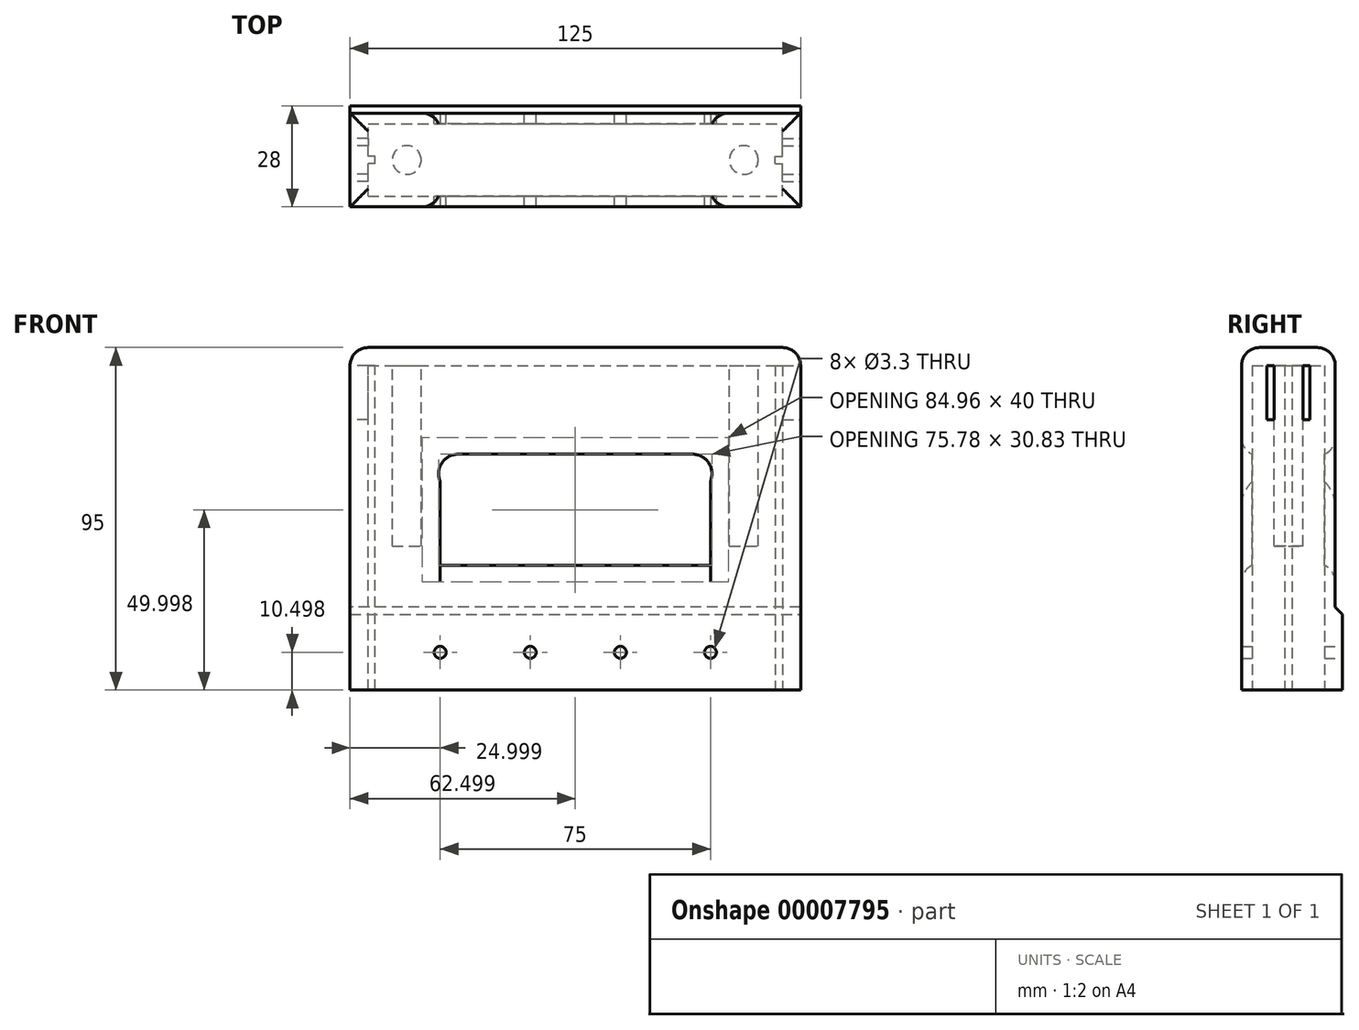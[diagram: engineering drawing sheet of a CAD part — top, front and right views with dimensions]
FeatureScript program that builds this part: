
annotation { "Feature Type Name" : "Feature", "Feature Type Description" : "" }
export const myFeature = defineFeature(function(context is Context, id is Id, definition is map)
    precondition{}
    {
        {
            var Q0;
            Q0=qCreatedBy(makeId("Front.planeOp"),FACE);
            var sketch = newSketch(context, id + "F0", { "sketchPlane" : qUnion([Q0])});
            skLineSegment(sketch, "E0.bottom", {"start": v(-53.4, 72.15) * mm, "end": v(71.6, 72.15) * mm});
            skLineSegment(sketch, "E0.top", {"start": v(-53.4, -22.85) * mm, "end": v(71.6, -22.85) * mm});
            skLineSegment(sketch, "E0.left", {"start": v(-53.4, 72.15) * mm, "end": v(-53.4, -22.85) * mm});
            skLineSegment(sketch, "E0.right", {"start": v(71.6, 72.15) * mm, "end": v(71.6, -22.85) * mm});
            skLineSegment(sketch, "E1.bottom", {"start": v(-28.4, 42.15) * mm, "end": v(46.6, 42.15) * mm});
            skLineSegment(sketch, "E1.top", {"start": v(-28.4, 12.15) * mm, "end": v(46.6, 12.15) * mm});
            skLineSegment(sketch, "E1.left", {"start": v(-28.4, 42.15) * mm, "end": v(-28.4, 12.15) * mm});
            skLineSegment(sketch, "E1.right", {"start": v(46.6, 42.15) * mm, "end": v(46.6, 12.15) * mm});
            skLineSegment(sketch, "E2", {"start": v(-28.4, 42.15) * mm, "end": v(-53.4, 42.15) * mm, "construction": true});
            skLineSegment(sketch, "E3", {"start": v(-28.4, 12.15) * mm, "end": v(-53.4, 12.15) * mm, "construction": true});
            skLineSegment(sketch, "E4", {"start": v(46.6, 42.15) * mm, "end": v(71.6, 42.15) * mm, "construction": true});
            skLineSegment(sketch, "E5", {"start": v(46.6, 12.15) * mm, "end": v(71.6, 12.15) * mm, "construction": true});
            skSolve(sketch);
        }
        {
            var Q0;
            Q0=makeQuery(id+"F0.imprint","IMPRINT",FACE,{"disambiguationData":[TD([[makeQuery(id+"F0.imprint","IMPRINT",EDGE,{"derivedFrom":sQuery(id+"F0.wireOp",EDGE,"E0.bottom")}),-1.0]])]});
            extrude(context, id + "F1", {"entities" : qUnion([Q0]), "depth" : 26 * mm});
        }
        {
            var Q0;
            Q0=makeQuery(id+"F1.opExtrude","SWEPT_FACE",FACE,{"disambiguationData":[OSD([sQuery(id+"F0.wireOp",EDGE,"E0.bottom")])]});
            fillet(context, id + "F2", {"entities" : qUnion([Q0]), "radius" : 5 * mm, "tangentPropagation" : true, "allowEdgeOverflow" : false});
        }
        {
            var Q0;
            Q0=makeQuery(id+"F1.opExtrude","SWEPT_FACE",FACE,{"disambiguationData":[OSD([sQuery(id+"F0.wireOp",EDGE,"E1.bottom")])]});
            var Q1;
            Q1=makeQuery(id+"F1.opExtrude","CAP_EDGE",EDGE,{"disambiguationData":[OSD([sQuery(id+"F0.wireOp",EDGE,"E1.top")])],"isStart":false});
            var Q2;
            Q2=makeQuery(id+"F1.opExtrude","CAP_EDGE",EDGE,{"disambiguationData":[OSD([sQuery(id+"F0.wireOp",EDGE,"E1.top")])],"isStart":true});
            fillet(context, id + "F3", {"entities" : qUnion([Q0, Q1, Q2]), "radius" : 5 * mm, "tangentPropagation" : true, "allowEdgeOverflow" : false});
        }
        {
            var Q0;
            Q0=makeQuery(id+"F1.opExtrude","SWEPT_FACE",FACE,{"disambiguationData":[OSD([sQuery(id+"F0.wireOp",EDGE,"E0.top")])]});
            var sketch = newSketch(context, id + "F4", { "sketchPlane" : qUnion([Q0])});
            skLineSegment(sketch, "E6.bottom", {"start": v(-48.4, 23) * mm, "end": v(66.6, 23) * mm});
            skLineSegment(sketch, "E6.top", {"start": v(-48.4, 3) * mm, "end": v(66.6, 3) * mm});
            skLineSegment(sketch, "E6.left", {"start": v(-48.4, 23) * mm, "end": v(-48.4, 3) * mm});
            skLineSegment(sketch, "E6.right", {"start": v(66.6, 23) * mm, "end": v(66.6, 3) * mm});
            skLineSegment(sketch, "E7.0", {"start": v(-53.4, 26) * mm, "end": v(-53.4, 0) * mm});
            skLineSegment(sketch, "E8.0", {"start": v(-53.4, 26) * mm, "end": v(71.6, 26) * mm});
            skLineSegment(sketch, "E9.0", {"start": v(71.6, 26) * mm, "end": v(71.6, 0) * mm});
            skLineSegment(sketch, "E10.0", {"start": v(-53.4, 0) * mm, "end": v(71.6, 0) * mm});
            skLineSegment(sketch, "E11", {"start": v(-48.4, 23) * mm, "end": v(-53.4, 23) * mm, "construction": true});
            skLineSegment(sketch, "E12", {"start": v(-48.4, 23) * mm, "end": v(-48.4, 26) * mm, "construction": true});
            skLineSegment(sketch, "E13", {"start": v(66.6, 23) * mm, "end": v(71.6, 23) * mm, "construction": true});
            skSolve(sketch);
        }
        {
            var Q0;
            Q0=makeQuery(id+"F4.imprint","IMPRINT",FACE,{"disambiguationData":[TD([[makeQuery(id+"F4.imprint","IMPRINT",EDGE,{"derivedFrom":sQuery(id+"F4.wireOp",EDGE,"E6.bottom")}),-1.0]])]});
            extrude(context, id + "F5", {"entities" : qUnion([Q0]), "operationType" : NewBodyOperationType.REMOVE, "oppositeDirection" : true, "depth" : 90 * mm});
        }
        {
            var Q0;
            Q0=makeQuery(id+"F1.opExtrude","CAP_FACE",FACE,{"disambiguationData":[OSD([sQuery(id+"F0.wireOp",EDGE,"E0.bottom"),sQuery(id+"F0.wireOp",EDGE,"E0.top"),sQuery(id+"F0.wireOp",EDGE,"E0.left"),sQuery(id+"F0.wireOp",EDGE,"E0.right"),sQuery(id+"F0.wireOp",EDGE,"E1.bottom"),sQuery(id+"F0.wireOp",EDGE,"E1.top"),sQuery(id+"F0.wireOp",EDGE,"E1.left"),sQuery(id+"F0.wireOp",EDGE,"E1.right")])],"isStart":true});
            var sketch = newSketch(context, id + "F6", { "sketchPlane" : qUnion([Q0])});
            skLineSegment(sketch, "E14.bottom", {"start": v(-71.6, 0.15) * mm, "end": v(53.4, 0.15) * mm});
            skLineSegment(sketch, "E14.top", {"start": v(-71.6, -22.85) * mm, "end": v(53.4, -22.85) * mm});
            skLineSegment(sketch, "E14.left", {"start": v(-71.6, 0.15) * mm, "end": v(-71.6, -22.85) * mm});
            skLineSegment(sketch, "E14.right", {"start": v(53.4, 0.15) * mm, "end": v(53.4, -22.85) * mm});
            skLineSegment(sketch, "E15.0", {"start": v(53.4, -22.85) * mm, "end": v(-71.6, -22.85) * mm});
            skSolve(sketch);
        }
        {
            var Q0;
            Q0 = qSketchRegion(id + "F6", true);
            extrude(context, id + "F7", {"entities" : qUnion([Q0]), "operationType" : NewBodyOperationType.ADD, "depth" : 2 * mm});
        }
        {
            var Q0;
            Q0=makeQuery(id+"F7.opExtrude","CAP_EDGE",EDGE,{"disambiguationData":[OSD([sQuery(id+"F6.wireOp",EDGE,"E14.bottom")])],"isStart":false});
            chamfer(context, id + "F8", {"entities" : qUnion([Q0]), "width" : 2 * mm, "tangentPropagation" : true});
        }
        {
            var Q0;
            Q0=makeQuery(id+"F5.boolean.opBoolean","COPY",FACE,{"derivedFrom":makeQuery(id+"F5.opExtrude","SWEPT_FACE",FACE,{"disambiguationData":[OSD([sQuery(id+"F4.wireOp",EDGE,"E6.left")])]})});
            var sketch = newSketch(context, id + "F9", { "sketchPlane" : qUnion([Q0])});
            skLineSegment(sketch, "E16.0", {"start": v(-23, -22.85) * mm, "end": v(-3, -22.85) * mm, "construction": true});
            skLineSegment(sketch, "E17", {"start": v(-14, -22.85) * mm, "end": v(-14, 67.15) * mm});
            skLineSegment(sketch, "E18", {"start": v(-12, -22.85) * mm, "end": v(-12, 67.15) * mm});
            skLineSegment(sketch, "E19", {"start": v(-14, 67.15) * mm, "end": v(-12, 67.15) * mm});
            skLineSegment(sketch, "E20", {"start": v(-14, -22.85) * mm, "end": v(-12, -22.85) * mm});
            skSolve(sketch);
        }
        {
            var Q0;
            Q0 = qSketchRegion(id + "F9", true);
            extrude(context, id + "F10", {"entities" : qUnion([Q0]), "operationType" : NewBodyOperationType.ADD, "depth" : 2 * mm});
        }
        {
            var Q0;
            Q0=makeQuery(id+"F5.boolean.opBoolean","COPY",FACE,{"derivedFrom":makeQuery(id+"F5.opExtrude","SWEPT_FACE",FACE,{"disambiguationData":[OSD([sQuery(id+"F4.wireOp",EDGE,"E6.right")])]})});
            var sketch = newSketch(context, id + "F11", { "sketchPlane" : qUnion([Q0])});
            skLineSegment(sketch, "E21.0", {"start": v(23, -22.85) * mm, "end": v(3, -22.85) * mm});
            skLineSegment(sketch, "E22.0", {"start": v(23, 67.15) * mm, "end": v(3, 67.15) * mm});
            skLineSegment(sketch, "E23", {"start": v(12, 67.15) * mm, "end": v(12, -22.85) * mm});
            skLineSegment(sketch, "E24", {"start": v(14, 67.15) * mm, "end": v(14, -22.85) * mm});
            skLineSegment(sketch, "E25", {"start": v(12, 67.15) * mm, "end": v(14, 67.15) * mm});
            skLineSegment(sketch, "E26", {"start": v(12, -22.85) * mm, "end": v(14, -22.85) * mm});
            skSolve(sketch);
        }
        {
            var Q0;
            Q0 = qSketchRegion(id + "F11", true);
            extrude(context, id + "F12", {"entities" : qUnion([Q0]), "operationType" : NewBodyOperationType.ADD, "depth" : 2 * mm});
        }
        {
            var Q0;
            Q0=makeQuery(id+"F5.boolean.opBoolean","COPY",FACE,{"derivedFrom":makeQuery(id+"F5.opExtrude","CAP_FACE",FACE,{"disambiguationData":[OSD([sQuery(id+"F4.wireOp",EDGE,"E6.bottom"),sQuery(id+"F4.wireOp",EDGE,"E6.top"),sQuery(id+"F4.wireOp",EDGE,"E6.left"),sQuery(id+"F4.wireOp",EDGE,"E6.right")])],"isStart":false})});
            var sketch = newSketch(context, id + "F13", { "sketchPlane" : qUnion([Q0])});
            skLineSegment(sketch, "E27.0", {"start": v(-46.4, 14) * mm, "end": v(-46.4, 12) * mm});
            skLineSegment(sketch, "E28.0", {"start": v(64.6, 14) * mm, "end": v(64.6, 12) * mm});
            skPoint(sketch, "E29", {"position": v(-46.4, 13) * mm});
            skPoint(sketch, "E30", {"position": v(64.6, 13) * mm});
            skLineSegment(sketch, "E31", {"start": v(64.6, 13) * mm, "end": v(-46.4, 13) * mm, "construction": true});
            skPoint(sketch, "E32", {"position": v(-37.65, 13) * mm});
            skPoint(sketch, "E33", {"position": v(55.85, 13) * mm});
            skCircle(sketch, "E34", {"center": v(-37.65, 13) * mm, "radius": 4 * mm});
            skCircle(sketch, "E35", {"center": v(55.85, 13) * mm, "radius": 4 * mm});
            skSolve(sketch);
        }
        {
            var Q0;
            Q0 = qSketchRegion(id + "F13", true);
            extrude(context, id + "F14", {"entities" : qUnion([Q0]), "operationType" : NewBodyOperationType.ADD, "depth" : 50 * mm});
        }
        {
            var Q0;
            Q0=makeQuery(id+"F7.opExtrude","CAP_FACE",FACE,{"disambiguationData":[OSD([sQuery(id+"F6.wireOp",EDGE,"E14.bottom"),sQuery(id+"F6.wireOp",EDGE,"E14.left"),sQuery(id+"F6.wireOp",EDGE,"E14.right"),sQuery(id+"F6.wireOp",EDGE,"E15.0")])],"isStart":false});
            var sketch = newSketch(context, id + "F15", { "sketchPlane" : qUnion([Q0])});
            skLineSegment(sketch, "E36.0", {"start": v(-71.6, -1.85) * mm, "end": v(-71.6, -22.85) * mm});
            skLineSegment(sketch, "E37.0", {"start": v(-71.6, -1.85) * mm, "end": v(53.4, -1.85) * mm});
            skLineSegment(sketch, "E38.0", {"start": v(53.4, -22.85) * mm, "end": v(-71.6, -22.85) * mm});
            skLineSegment(sketch, "E39.0", {"start": v(53.4, -1.85) * mm, "end": v(53.4, -22.85) * mm});
            skPoint(sketch, "E40", {"position": v(-71.6, -12.35) * mm});
            skPoint(sketch, "E41", {"position": v(53.4, -12.35) * mm});
            skLineSegment(sketch, "E42", {"start": v(-71.6, -12.35) * mm, "end": v(53.4, -12.35) * mm, "construction": true});
            skPoint(sketch, "E43", {"position": v(-46.6, -12.35) * mm});
            skPoint(sketch, "E44", {"position": v(-21.6, -12.35) * mm});
            skPoint(sketch, "E45", {"position": v(3.4, -12.35) * mm});
            skPoint(sketch, "E46", {"position": v(28.4, -12.35) * mm});
            skCircle(sketch, "E47", {"center": v(-46.6, -12.35) * mm, "radius": 1.65 * mm});
            skCircle(sketch, "E48", {"center": v(-21.6, -12.35) * mm, "radius": 1.65 * mm});
            skCircle(sketch, "E49", {"center": v(3.4, -12.35) * mm, "radius": 1.65 * mm});
            skCircle(sketch, "E50", {"center": v(28.4, -12.35) * mm, "radius": 1.65 * mm});
            skSolve(sketch);
        }
        {
            var Q0;
            Q0=makeQuery(id+"F15.imprint","IMPRINT",FACE,{"disambiguationData":[TD([[makeQuery(id+"F15.imprint","IMPRINT",EDGE,{"derivedFrom":sQuery(id+"F15.wireOp",EDGE,"E47")}),1.0]])]});
            var Q1;
            Q1=makeQuery(id+"F15.imprint","IMPRINT",FACE,{"disambiguationData":[TD([[makeQuery(id+"F15.imprint","IMPRINT",EDGE,{"derivedFrom":sQuery(id+"F15.wireOp",EDGE,"E48")}),1.0]])]});
            var Q2;
            Q2=makeQuery(id+"F15.imprint","IMPRINT",FACE,{"disambiguationData":[TD([[makeQuery(id+"F15.imprint","IMPRINT",EDGE,{"derivedFrom":sQuery(id+"F15.wireOp",EDGE,"E49")}),1.0]])]});
            var Q3;
            Q3=makeQuery(id+"F15.imprint","IMPRINT",FACE,{"disambiguationData":[TD([[makeQuery(id+"F15.imprint","IMPRINT",EDGE,{"derivedFrom":sQuery(id+"F15.wireOp",EDGE,"E50")}),1.0]])]});
            extrude(context, id + "F16", {"entities" : qUnion([Q0, Q1, Q2, Q3]), "operationType" : NewBodyOperationType.REMOVE, "endBound" : BoundingType.THROUGH_ALL, "oppositeDirection" : true, "depth" : 27.5 * mm});
        }
        {
            var Q0;
            Q0=makeQuery(id+"F7.boolean.opBoolean","MERGE",FACE,{"derivedFrom":[makeQuery(id+"F1.opExtrude","SWEPT_FACE",FACE,{"disambiguationData":[OSD([sQuery(id+"F0.wireOp",EDGE,"E0.right")])]}),makeQuery(id+"F7.opExtrude","SWEPT_FACE",FACE,{"disambiguationData":[OSD([sQuery(id+"F6.wireOp",EDGE,"E14.left")])]})]});
            var sketch = newSketch(context, id + "F17", { "sketchPlane" : qUnion([Q0])});
            skLineSegment(sketch, "E51.0", {"start": v(0, 67.15) * mm, "end": v(-26, 67.15) * mm});
            skPoint(sketch, "E52", {"position": v(-13, 67.15) * mm});
            skPoint(sketch, "E53", {"position": v(-9, 67.15) * mm});
            skPoint(sketch, "E54", {"position": v(-17, 67.15) * mm});
            skPoint(sketch, "E55", {"position": v(-19, 67.15) * mm});
            skPoint(sketch, "E56", {"position": v(-7, 67.15) * mm});
            skLineSegment(sketch, "E57", {"start": v(-19, 67.15) * mm, "end": v(-19, 52.15) * mm});
            skLineSegment(sketch, "E58", {"start": v(-17, 67.15) * mm, "end": v(-17, 52.15) * mm});
            skLineSegment(sketch, "E59", {"start": v(-9, 67.15) * mm, "end": v(-9, 52.15) * mm});
            skLineSegment(sketch, "E60", {"start": v(-7, 67.15) * mm, "end": v(-7, 52.15) * mm});
            skLineSegment(sketch, "E61", {"start": v(-19, 52.15) * mm, "end": v(-17, 52.15) * mm});
            skLineSegment(sketch, "E62", {"start": v(-9, 52.15) * mm, "end": v(-7, 52.15) * mm});
            skSolve(sketch);
        }
        {
            var Q0;
            {var subQ1=sQuery(id+"F17.wireOp",EDGE,"E57");Q0=makeQuery(id+"F17.imprint","IMPRINT",FACE,{"disambiguationData":[TD([[makeQuery(id+"F17.imprint","IMPRINT",EDGE,{"derivedFrom":subQ1}),1.0]])]});}
            var Q1;
            {var subQ1=sQuery(id+"F17.wireOp",EDGE,"E59");Q1=makeQuery(id+"F17.imprint","IMPRINT",FACE,{"disambiguationData":[TD([[makeQuery(id+"F17.imprint","IMPRINT",EDGE,{"derivedFrom":subQ1}),1.0]])]});}
            extrude(context, id + "F18", {"entities" : qUnion([Q0, Q1]), "operationType" : NewBodyOperationType.REMOVE, "endBound" : BoundingType.UP_TO_NEXT, "oppositeDirection" : true, "depth" : 25 * mm});
        }
        {
            var Q0;
            Q0=makeQuery(id+"F7.boolean.opBoolean","MERGE",FACE,{"derivedFrom":[makeQuery(id+"F1.opExtrude","SWEPT_FACE",FACE,{"disambiguationData":[OSD([sQuery(id+"F0.wireOp",EDGE,"E0.left")])]}),makeQuery(id+"F7.opExtrude","SWEPT_FACE",FACE,{"disambiguationData":[OSD([sQuery(id+"F6.wireOp",EDGE,"E14.right")])]})]});
            var sketch = newSketch(context, id + "F19", { "sketchPlane" : qUnion([Q0])});
            skLineSegment(sketch, "E63.0", {"start": v(26, 67.15) * mm, "end": v(0, 67.15) * mm});
            skPoint(sketch, "E64", {"position": v(13, 67.15) * mm});
            skLineSegment(sketch, "E65", {"start": v(13, 67.15) * mm, "end": v(13, -22.85) * mm, "construction": true});
            skPoint(sketch, "E66", {"position": v(17, 67.15) * mm});
            skPoint(sketch, "E67", {"position": v(19, 67.15) * mm});
            skLineSegment(sketch, "E68", {"start": v(19, 67.15) * mm, "end": v(19, 52.15) * mm});
            skLineSegment(sketch, "E69", {"start": v(17, 67.15) * mm, "end": v(17, 52.15) * mm});
            skLineSegment(sketch, "E70", {"start": v(17, 52.15) * mm, "end": v(19, 52.15) * mm});
            skLineSegment(sketch, "E71.MirrorCS", {"start": v(9, 67.15) * mm, "end": v(9, 52.15) * mm});
            skLineSegment(sketch, "E72.MirrorCS", {"start": v(7, 67.15) * mm, "end": v(7, 52.15) * mm});
            skLineSegment(sketch, "E73.MirrorCS", {"start": v(9, 52.15) * mm, "end": v(7, 52.15) * mm});
            skSolve(sketch);
        }
        {
            var Q0;
            {var subQ1=sQuery(id+"F19.wireOp",EDGE,"E71.MirrorCS");Q0=makeQuery(id+"F19.imprint","IMPRINT",FACE,{"disambiguationData":[TD([[makeQuery(id+"F19.imprint","IMPRINT",EDGE,{"derivedFrom":subQ1}),-1.0]])]});}
            var Q1;
            {var subQ1=sQuery(id+"F19.wireOp",EDGE,"E68");Q1=makeQuery(id+"F19.imprint","IMPRINT",FACE,{"disambiguationData":[TD([[makeQuery(id+"F19.imprint","IMPRINT",EDGE,{"derivedFrom":subQ1}),-1.0]])]});}
            extrude(context, id + "F20", {"entities" : qUnion([Q0, Q1]), "operationType" : NewBodyOperationType.REMOVE, "endBound" : BoundingType.UP_TO_NEXT, "oppositeDirection" : true, "depth" : 25 * mm});
        }
    });
